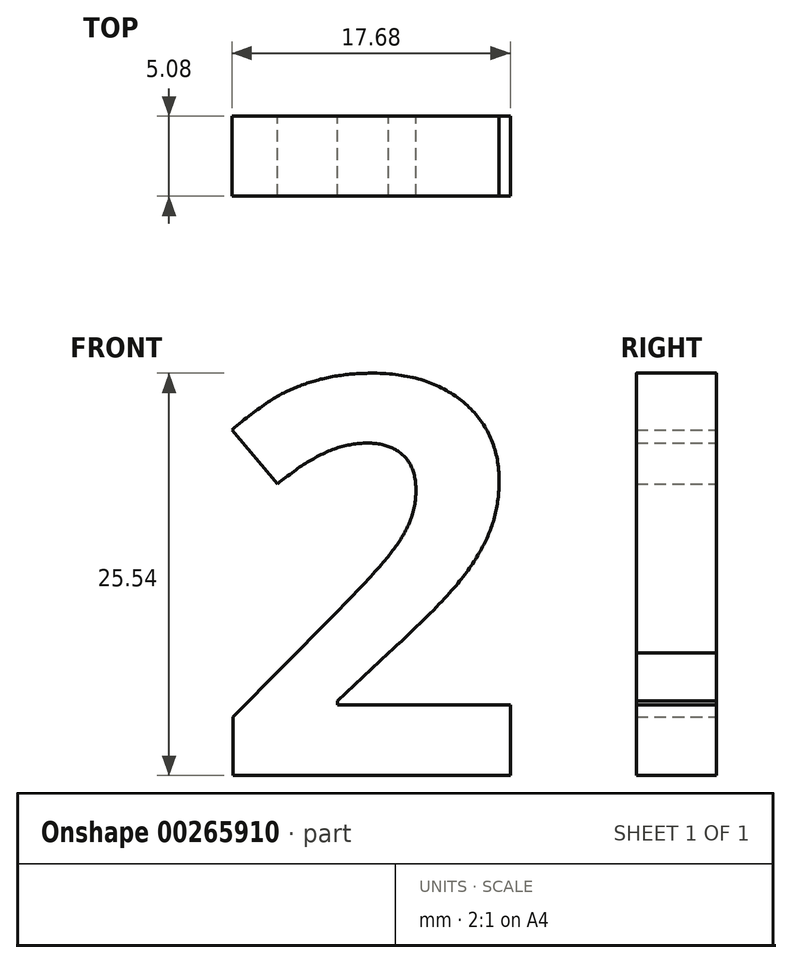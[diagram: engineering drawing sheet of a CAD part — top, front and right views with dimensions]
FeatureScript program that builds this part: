
annotation { "Feature Type Name" : "Feature", "Feature Type Description" : "" }
export const myFeature = defineFeature(function(context is Context, id is Id, definition is map)
    precondition{}
    {
        {
            var Q0;
            Q0=qCreatedBy(makeId("Front.planeOp"),FACE);
            var sketch = newSketch(context, id + "F0", { "sketchPlane" : qUnion([Q0])});
            skText(sketch, "E0", { "text": "2", "fontName": "OpenSans-Bold.ttf"});
            const initialGuessF0  = {"E0": [-0.0213, 0.03733, 1, 0, 0.0254]};
            skSetInitialGuess(sketch, initialGuessF0);
            skSolve(sketch);
        }
        {
            var Q0;
            Q0 = qSketchRegion(id + "F0", true);
            extrude(context, id + "F1", {"entities" : qUnion([Q0]), "depth" : 5.08 * mm});
        }
    });
